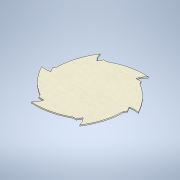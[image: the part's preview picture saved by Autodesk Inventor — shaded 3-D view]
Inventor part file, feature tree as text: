
AUTODESK INVENTOR PART (.ipt)
format: ipt  version: 2021 (Build 250183000, 183)  size: 138,240 bytes
history: native  units: mm
features: extrude x1, sketch x1
ambient origin geometry x8: Origin, YZ Plane, XZ Plane, XY Plane, X Axis, Y Axis, Z Axis, Center Point
bodies: Solid1 (feature_tree)
feature tree (2):
  extrude  "Extrusion1"  Depth=1.7mm TaperAngle=0.0deg
  sketch  "Sketch1"  dims[d0=101.0mm d1=1.7mm d2=0.0mm d17=60.0mm d19=360.0deg]
